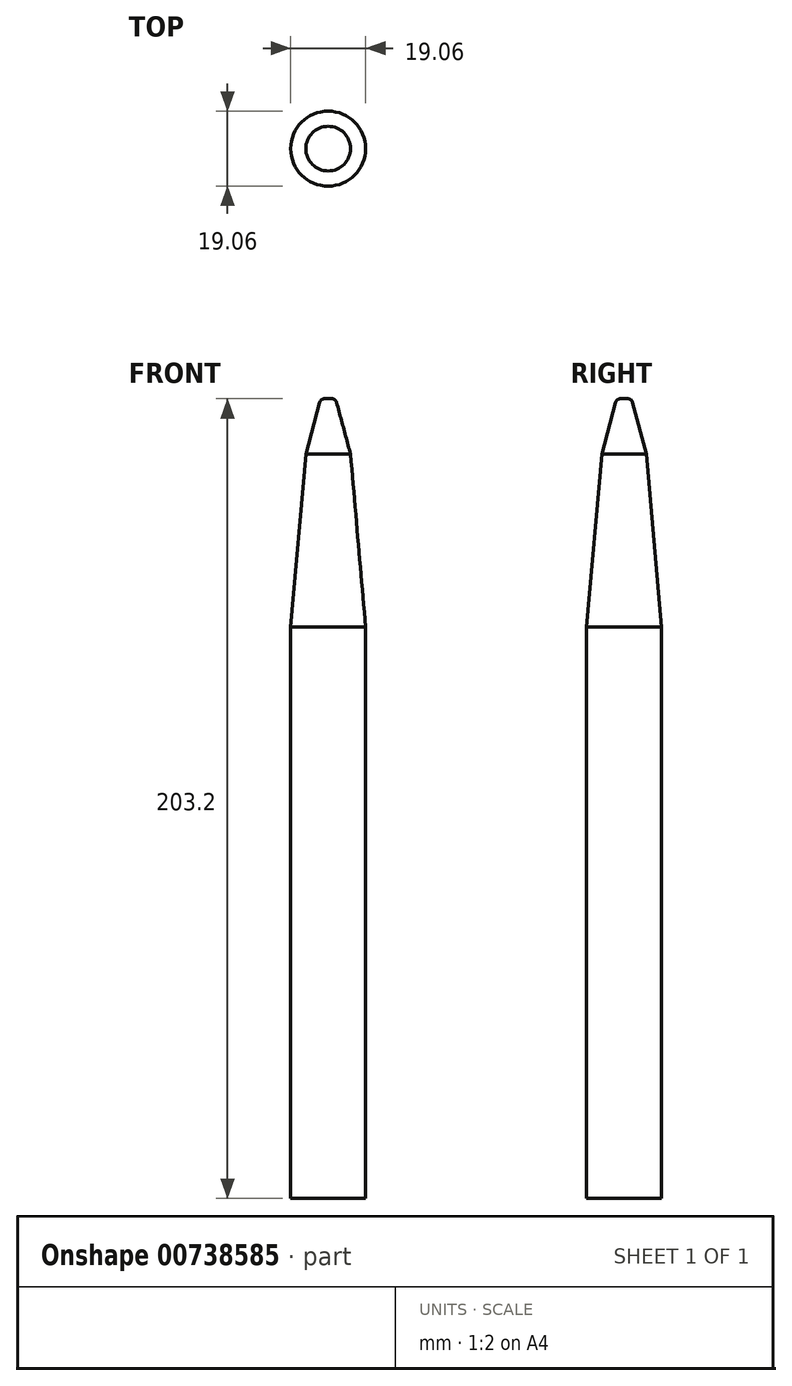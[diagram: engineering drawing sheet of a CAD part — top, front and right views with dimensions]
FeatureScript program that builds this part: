
annotation { "Feature Type Name" : "Feature", "Feature Type Description" : "" }
export const myFeature = defineFeature(function(context is Context, id is Id, definition is map)
    precondition{}
    {
        {
            var Q0;
            Q0=qCreatedBy(makeId("Top.planeOp"),FACE);
            var sketch = newSketch(context, id + "F0", { "sketchPlane" : qUnion([Q0])});
            skCircle(sketch, "E0", {"center": v(0, 0) * mm, "radius": 9.53 * mm});
            skSolve(sketch);
        }
        {
            var Q0;
            Q0=makeQuery(id+"F0.imprint","IMPRINT",FACE,{"disambiguationData":[TD([[makeQuery(id+"F0.imprint","IMPRINT",EDGE,{"derivedFrom":sQuery(id+"F0.wireOp",EDGE,"E0")}),1.0]])]});
            extrude(context, id + "F1", {"entities" : qUnion([Q0]), "depth" : 203.2 * mm, "offsetDistance" : 25.4 * mm});
        }
        {
            var Q0;
            Q0=makeQuery(id+"F1.opExtrude","CAP_EDGE",EDGE,{"disambiguationData":[OSD([sQuery(id+"F0.wireOp",EDGE,"E0")])],"isStart":false});
            chamfer(context, id + "F2", {"entities" : qUnion([Q0]), "chamferType" : ChamferType.OFFSET_ANGLE, "width" : 5.08 * mm, "oppositeDirection" : false, "angle" : 85 * degree, "tangentPropagation" : true});
        }
        {
            var Q0;
            {var subQ0=sQuery(id+"F0.wireOp",EDGE,"E0");Q0=makeQuery(id+"F2.opChamfer","BLEND_EDGE",EDGE,{"blendedFrom":[makeQuery(id+"F1.opExtrude","CAP_EDGE",EDGE,{"disambiguationData":[OSD([subQ0])],"isStart":false}),makeQuery(id+"F1.opExtrude","CAP_FACE",FACE,{"disambiguationData":[OSD([subQ0])],"isStart":false})],"blendedInto":[makeQuery(id+"F1.opExtrude","CAP_FACE",FACE,{"disambiguationData":[OSD([subQ0])],"isStart":false})]});}
            chamfer(context, id + "F3", {"entities" : qUnion([Q0]), "chamferType" : ChamferType.OFFSET_ANGLE, "width" : 2.54 * mm, "oppositeDirection" : false, "angle" : 75 * degree, "tangentPropagation" : true});
        }
        {
            var Q0;
            {var subQ0=sQuery(id+"F0.wireOp",EDGE,"E0");var subQ1=makeQuery(id+"F1.opExtrude","CAP_FACE",FACE,{"disambiguationData":[OSD([subQ0])],"isStart":false});Q0=makeQuery(id+"F3.opChamfer","BLEND_EDGE",EDGE,{"blendedFrom":[makeQuery(id+"F2.opChamfer","BLEND_EDGE",EDGE,{"blendedFrom":[makeQuery(id+"F1.opExtrude","CAP_EDGE",EDGE,{"disambiguationData":[OSD([subQ0])],"isStart":false}),subQ1],"blendedInto":[subQ1]}),subQ1],"blendedInto":[subQ1]});}
            fillet(context, id + "F4", {"entities" : qUnion([Q0]), "radius" : 1.27 * mm, "tangentPropagation" : true, "allowEdgeOverflow" : false});
        }
    });
